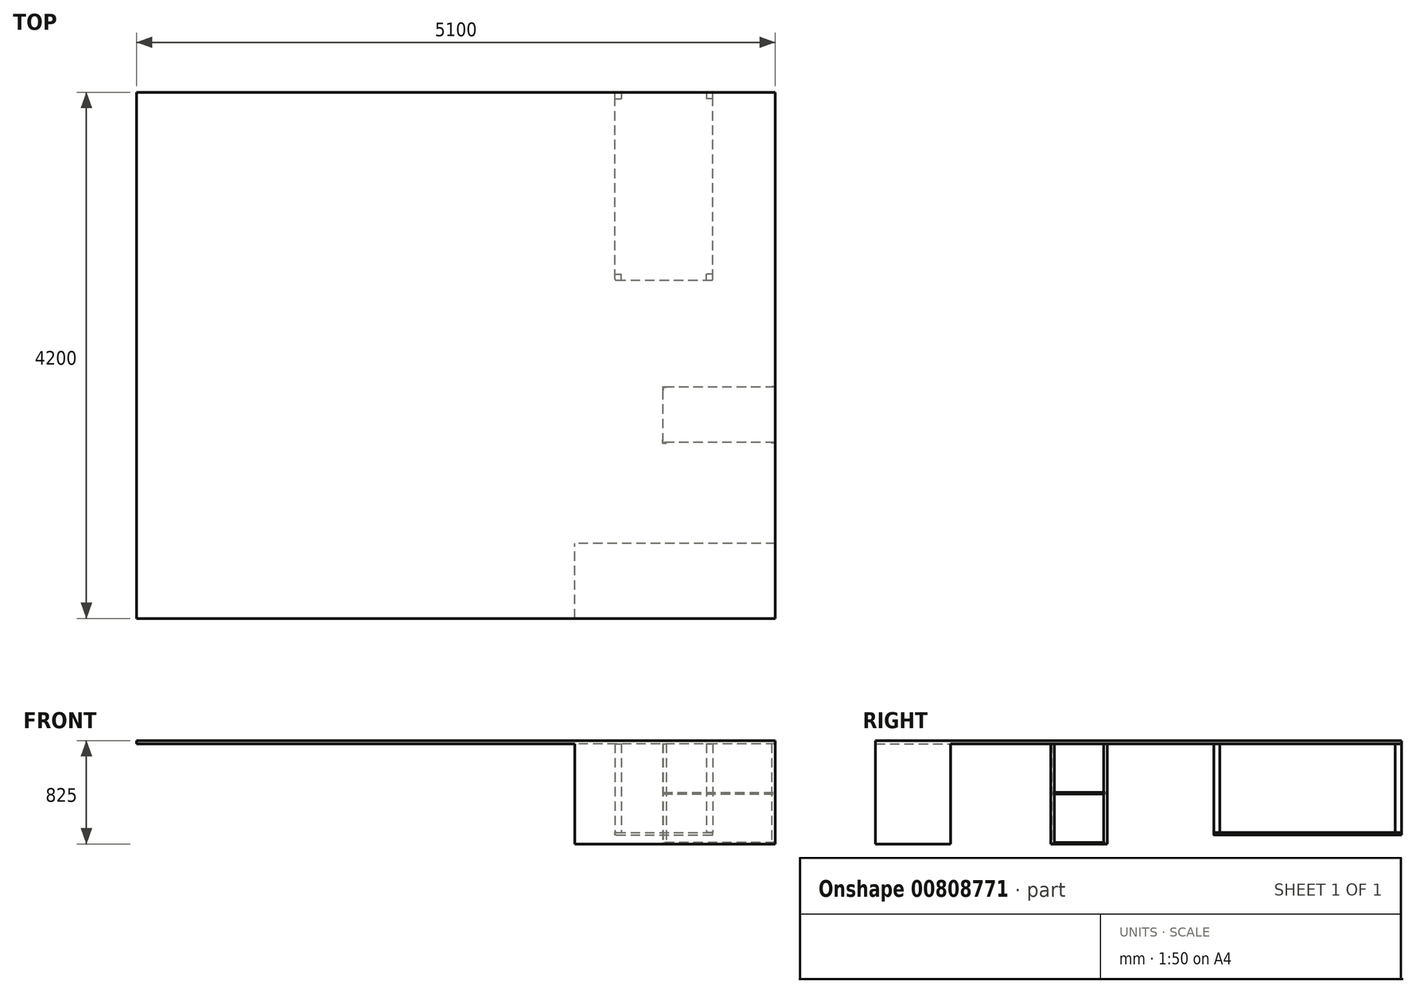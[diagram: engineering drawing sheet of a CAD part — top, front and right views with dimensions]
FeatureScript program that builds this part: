
annotation { "Feature Type Name" : "Feature", "Feature Type Description" : "" }
export const myFeature = defineFeature(function(context is Context, id is Id, definition is map)
    precondition{}
    {
        {
            var Q0;
            Q0=qCreatedBy(makeId("Top.planeOp"),FACE);
            var sketch = newSketch(context, id + "F0", { "sketchPlane" : qUnion([Q0])});
            skPoint(sketch, "E0.middle", {"position": v(0, 0) * mm});
            skLineSegment(sketch, "E1", {"start": v(-450, 225) * mm, "end": v(-450, 196) * mm});
            skLineSegment(sketch, "E2", {"start": v(-450, 225) * mm, "end": v(-421, 225) * mm});
            skLineSegment(sketch, "E3.0", {"start": v(-446, 221) * mm, "end": v(-421, 221) * mm});
            skLineSegment(sketch, "E3.1", {"start": v(-446, 221) * mm, "end": v(-446, 196) * mm});
            skLineSegment(sketch, "E4", {"start": v(-421, 225) * mm, "end": v(-421, 221) * mm});
            skLineSegment(sketch, "E5", {"start": v(-446, 196) * mm, "end": v(-450, 196) * mm});
            skLineSegment(sketch, "E6.bottom", {"start": v(0, 0) * mm, "end": v(-19.98, 0) * mm, "construction": true});
            skLineSegment(sketch, "E6.top", {"start": v(0, 2.25) * mm, "end": v(-19.98, 2.25) * mm, "construction": true});
            skLineSegment(sketch, "E6.left", {"start": v(0, 0) * mm, "end": v(0, 2.25) * mm, "construction": true});
            skLineSegment(sketch, "E6.right", {"start": v(-19.98, 0) * mm, "end": v(-19.98, 2.25) * mm, "construction": true});
            skLineSegment(sketch, "E7.MirrorCS", {"start": v(-446, -196) * mm, "end": v(-450, -196) * mm});
            skLineSegment(sketch, "E8.MirrorCS", {"start": v(-421, -225) * mm, "end": v(-421, -221) * mm});
            skLineSegment(sketch, "E9.MirrorCS", {"start": v(-450, -225) * mm, "end": v(-421, -225) * mm});
            skLineSegment(sketch, "E10.MirrorCS", {"start": v(-450, -225) * mm, "end": v(-450, -196) * mm});
            skLineSegment(sketch, "E11.MirrorCS", {"start": v(-446, -221) * mm, "end": v(-421, -221) * mm});
            skLineSegment(sketch, "E12.MirrorCS", {"start": v(-446, -221) * mm, "end": v(-446, -196) * mm});
            skLineSegment(sketch, "E13.MirrorCS", {"start": v(421, -225) * mm, "end": v(421, -221) * mm});
            skLineSegment(sketch, "E14.MirrorCS", {"start": v(446, -221) * mm, "end": v(421, -221) * mm});
            skLineSegment(sketch, "E15.MirrorCS", {"start": v(450, -225) * mm, "end": v(421, -225) * mm});
            skLineSegment(sketch, "E16.MirrorCS", {"start": v(446, -196) * mm, "end": v(450, -196) * mm});
            skLineSegment(sketch, "E17.MirrorCS", {"start": v(450, 225) * mm, "end": v(450, 196) * mm});
            skLineSegment(sketch, "E18.MirrorCS", {"start": v(446, 196) * mm, "end": v(450, 196) * mm});
            skLineSegment(sketch, "E19.MirrorCS", {"start": v(446, 221) * mm, "end": v(446, 196) * mm});
            skLineSegment(sketch, "E20.MirrorCS", {"start": v(446, 221) * mm, "end": v(421, 221) * mm});
            skLineSegment(sketch, "E21.MirrorCS", {"start": v(450, 225) * mm, "end": v(421, 225) * mm});
            skLineSegment(sketch, "E22.MirrorCS", {"start": v(450, -225) * mm, "end": v(450, -196) * mm});
            skLineSegment(sketch, "E23.MirrorCS", {"start": v(446, -221) * mm, "end": v(446, -196) * mm});
            skLineSegment(sketch, "E24.MirrorCS", {"start": v(421, 225) * mm, "end": v(421, 221) * mm});
            skSolve(sketch);
        }
        {
            var Q0;
            Q0 = qSketchRegion(id + "F0", true);
            extrude(context, id + "F1", {"entities" : qUnion([Q0]), "depth" : 800 * mm, "offsetDistance" : 25 * mm});
        }
        {
            var Q0;
            Q0=makeQuery(id+"F1.opExtrude","CAP_FACE",FACE,{"disambiguationData":[OSD([sQuery(id+"F0.wireOp",EDGE,"E13.MirrorCS"),sQuery(id+"F0.wireOp",EDGE,"E14.MirrorCS"),sQuery(id+"F0.wireOp",EDGE,"E15.MirrorCS"),sQuery(id+"F0.wireOp",EDGE,"E16.MirrorCS"),sQuery(id+"F0.wireOp",EDGE,"E22.MirrorCS"),sQuery(id+"F0.wireOp",EDGE,"E23.MirrorCS")])],"isStart":true});
            var sketch = newSketch(context, id + "F2", { "sketchPlane" : qUnion([Q0])});
            skLineSegment(sketch, "E25.bottom", {"start": v(446, 221) * mm, "end": v(-446, 221) * mm});
            skLineSegment(sketch, "E25.top", {"start": v(446, -221) * mm, "end": v(-446, -221) * mm});
            skLineSegment(sketch, "E25.left", {"start": v(446, 221) * mm, "end": v(446, -221) * mm});
            skLineSegment(sketch, "E25.right", {"start": v(-446, 221) * mm, "end": v(-446, -221) * mm});
            skSolve(sketch);
        }
        {
            var Q0;
            Q0 = qSketchRegion(id + "F2", true);
            extrude(context, id + "F3", {"entities" : qUnion([Q0]), "oppositeDirection" : true, "depth" : 10 * mm, "offsetDistance" : 25 * mm});
        }
        {
            var Q0;
            Q0=makeQuery(id+"F3.opExtrude","CAP_FACE",FACE,{"disambiguationData":[OSD([sQuery(id+"F2.wireOp",EDGE,"E25.bottom"),sQuery(id+"F2.wireOp",EDGE,"E25.top"),sQuery(id+"F2.wireOp",EDGE,"E25.left"),sQuery(id+"F2.wireOp",EDGE,"E25.right")])],"isStart":true});
            cPlane(context, id + "F4", {"entities" : qUnion([Q0]), "cplaneType" : CPlaneType.OFFSET, "offset" : 400 * mm, "oppositeDirection" : true, "width" : 150 * mm, "height" : 150 * mm});
        }
        {
            var Q0;
            Q0=qCreatedBy(id+"F4.planeOp",FACE);
            var sketch = newSketch(context, id + "F5", { "sketchPlane" : qUnion([Q0])});
            skLineSegment(sketch, "E26.0", {"start": v(446, -221) * mm, "end": v(446, 221) * mm});
            skLineSegment(sketch, "E26.1", {"start": v(-446, -221) * mm, "end": v(446, -221) * mm});
            skLineSegment(sketch, "E26.2", {"start": v(-446, 221) * mm, "end": v(-446, -221) * mm});
            skLineSegment(sketch, "E26.3", {"start": v(446, 221) * mm, "end": v(-446, 221) * mm});
            skSolve(sketch);
        }
        {
            var Q0;
            Q0 = qSketchRegion(id + "F5", true);
            extrude(context, id + "F6", {"entities" : qUnion([Q0]), "oppositeDirection" : true, "depth" : 10 * mm, "offsetDistance" : 25 * mm});
        }
        {
            var Q0;
            Q0=makeQuery(id+"F1.opExtrude","CAP_FACE",FACE,{"disambiguationData":[OSD([sQuery(id+"F0.wireOp",EDGE,"E1"),sQuery(id+"F0.wireOp",EDGE,"E2"),sQuery(id+"F0.wireOp",EDGE,"E3.0"),sQuery(id+"F0.wireOp",EDGE,"E3.1"),sQuery(id+"F0.wireOp",EDGE,"E4"),sQuery(id+"F0.wireOp",EDGE,"E5")])],"isStart":false});
            var sketch = newSketch(context, id + "F7", { "sketchPlane" : qUnion([Q0])});
            skLineSegment(sketch, "E27.bottom", {"start": v(450, 2575) * mm, "end": v(-4650, 2575) * mm});
            skLineSegment(sketch, "E27.top", {"start": v(450, -1625) * mm, "end": v(-4650, -1625) * mm});
            skLineSegment(sketch, "E27.left", {"start": v(450, 2575) * mm, "end": v(450, -1625) * mm});
            skLineSegment(sketch, "E27.right", {"start": v(-4650, 2575) * mm, "end": v(-4650, -1625) * mm});
            skLineSegment(sketch, "E28", {"start": v(450, -1025) * mm, "end": v(-4650, -1025) * mm, "construction": true});
            skSolve(sketch);
        }
        {
            var Q0;
            Q0 = qSketchRegion(id + "F7", true);
            extrude(context, id + "F8", {"entities" : qUnion([Q0]), "depth" : 25 * mm, "offsetDistance" : 25 * mm});
        }
        {
            var Q0;
            Q0=makeQuery(id+"F8.opExtrude","CAP_FACE",FACE,{"disambiguationData":[OSD([sQuery(id+"F7.wireOp",EDGE,"E27.bottom"),sQuery(id+"F7.wireOp",EDGE,"E27.top"),sQuery(id+"F7.wireOp",EDGE,"E27.left"),sQuery(id+"F7.wireOp",EDGE,"E27.right")])],"isStart":true});
            var sketch = newSketch(context, id + "F9", { "sketchPlane" : qUnion([Q0])});
            skLineSegment(sketch, "E29.bottom", {"start": v(450, 1625) * mm, "end": v(-1150, 1625) * mm});
            skLineSegment(sketch, "E29.top", {"start": v(450, 1025) * mm, "end": v(-1150, 1025) * mm});
            skLineSegment(sketch, "E29.left", {"start": v(450, 1625) * mm, "end": v(450, 1025) * mm});
            skLineSegment(sketch, "E29.right", {"start": v(-1150, 1625) * mm, "end": v(-1150, 1025) * mm});
            skSolve(sketch);
        }
        {
            var Q0;
            Q0 = qSketchRegion(id + "F9", true);
            extrude(context, id + "F10", {"entities" : qUnion([Q0]), "operationType" : NewBodyOperationType.ADD, "depth" : 800 * mm, "offsetDistance" : 25 * mm});
        }
        {
            var Q0;
            Q0=makeQuery(id+"F8.opExtrude","CAP_FACE",FACE,{"disambiguationData":[OSD([sQuery(id+"F7.wireOp",EDGE,"E27.bottom"),sQuery(id+"F7.wireOp",EDGE,"E27.top"),sQuery(id+"F7.wireOp",EDGE,"E27.left"),sQuery(id+"F7.wireOp",EDGE,"E27.right")])],"isStart":true});
            cPlane(context, id + "F11", {"entities" : qUnion([Q0]), "cplaneType" : CPlaneType.OFFSET, "offset" : 710 * mm, "width" : 150 * mm, "height" : 150 * mm});
        }
        {
            var Q0;
            Q0=qCreatedBy(id+"F11.planeOp",FACE);
            var sketch = newSketch(context, id + "F12", { "sketchPlane" : qUnion([Q0])});
            skLineSegment(sketch, "E30.bottom", {"start": v(-830, -1075) * mm, "end": v(-50, -1075) * mm});
            skLineSegment(sketch, "E30.top", {"start": v(-830, -2575) * mm, "end": v(-50, -2575) * mm});
            skLineSegment(sketch, "E30.left", {"start": v(-830, -1075) * mm, "end": v(-830, -2575) * mm});
            skLineSegment(sketch, "E30.right", {"start": v(-50, -1075) * mm, "end": v(-50, -2575) * mm});
            skSolve(sketch);
        }
        {
            var Q0;
            Q0 = qSketchRegion(id + "F12", true);
            extrude(context, id + "F13", {"entities" : qUnion([Q0]), "depth" : 18 * mm, "offsetDistance" : 25 * mm});
        }
        {
            var Q0;
            Q0=makeQuery(id+"F13.opExtrude","CAP_FACE",FACE,{"disambiguationData":[OSD([sQuery(id+"F12.wireOp",EDGE,"E30.bottom"),sQuery(id+"F12.wireOp",EDGE,"E30.top"),sQuery(id+"F12.wireOp",EDGE,"E30.left"),sQuery(id+"F12.wireOp",EDGE,"E30.right")])],"isStart":true});
            var sketch = newSketch(context, id + "F14", { "sketchPlane" : qUnion([Q0])});
            skLineSegment(sketch, "E31.bottom", {"start": v(-830, 1075) * mm, "end": v(-780, 1075) * mm});
            skLineSegment(sketch, "E31.top", {"start": v(-830, 1125) * mm, "end": v(-780, 1125) * mm});
            skLineSegment(sketch, "E31.left", {"start": v(-830, 1075) * mm, "end": v(-830, 1125) * mm});
            skLineSegment(sketch, "E31.right", {"start": v(-780, 1075) * mm, "end": v(-780, 1125) * mm});
            skLineSegment(sketch, "E32.bottom", {"start": v(-50, 1075) * mm, "end": v(-100, 1075) * mm});
            skLineSegment(sketch, "E32.top", {"start": v(-50, 1125) * mm, "end": v(-100, 1125) * mm});
            skLineSegment(sketch, "E32.left", {"start": v(-50, 1075) * mm, "end": v(-50, 1125) * mm});
            skLineSegment(sketch, "E32.right", {"start": v(-100, 1075) * mm, "end": v(-100, 1125) * mm});
            skLineSegment(sketch, "E33.bottom", {"start": v(-50, 2575) * mm, "end": v(-100, 2575) * mm});
            skLineSegment(sketch, "E33.top", {"start": v(-50, 2525) * mm, "end": v(-100, 2525) * mm});
            skLineSegment(sketch, "E33.left", {"start": v(-50, 2575) * mm, "end": v(-50, 2525) * mm});
            skLineSegment(sketch, "E33.right", {"start": v(-100, 2575) * mm, "end": v(-100, 2525) * mm});
            skLineSegment(sketch, "E34.bottom", {"start": v(-830, 2575) * mm, "end": v(-780, 2575) * mm});
            skLineSegment(sketch, "E34.top", {"start": v(-830, 2525) * mm, "end": v(-780, 2525) * mm});
            skLineSegment(sketch, "E34.left", {"start": v(-830, 2575) * mm, "end": v(-830, 2525) * mm});
            skLineSegment(sketch, "E34.right", {"start": v(-780, 2575) * mm, "end": v(-780, 2525) * mm});
            skSolve(sketch);
        }
        {
            var Q0;
            Q0 = qSketchRegion(id + "F14", true);
            var Q1;
            Q1=makeQuery(id+"F8.opExtrude","CAP_FACE",FACE,{"disambiguationData":[OSD([sQuery(id+"F7.wireOp",EDGE,"E27.bottom"),sQuery(id+"F7.wireOp",EDGE,"E27.top"),sQuery(id+"F7.wireOp",EDGE,"E27.left"),sQuery(id+"F7.wireOp",EDGE,"E27.right")])],"isStart":true});
            extrude(context, id + "F15", {"entities" : qUnion([Q0]), "endBound" : BoundingType.UP_TO_SURFACE, "depth" : 25 * mm, "endBoundEntityFace" : qUnion([Q1]), "offsetDistance" : 25 * mm});
        }
        {
            var Q0;
            Q0=makeQuery(id+"F13.opExtrude","SWEPT_EDGE",EDGE,{"disambiguationData":[OSD([sQuery(id+"F12.wireOp",EDGE,"E30.bottom"),sQuery(id+"F12.wireOp",EDGE,"E30.right")])]});
            var Q1;
            Q1=makeQuery(id+"F13.opExtrude","SWEPT_EDGE",EDGE,{"disambiguationData":[OSD([sQuery(id+"F12.wireOp",EDGE,"E30.top"),sQuery(id+"F12.wireOp",EDGE,"E30.right")])]});
            var Q2;
            Q2=makeQuery(id+"F13.opExtrude","SWEPT_EDGE",EDGE,{"disambiguationData":[OSD([sQuery(id+"F12.wireOp",EDGE,"E30.top"),sQuery(id+"F12.wireOp",EDGE,"E30.left")])]});
            var Q3;
            Q3=makeQuery(id+"F13.opExtrude","SWEPT_EDGE",EDGE,{"disambiguationData":[OSD([sQuery(id+"F12.wireOp",EDGE,"E30.bottom"),sQuery(id+"F12.wireOp",EDGE,"E30.left")])]});
            var Q4;
            Q4=makeQuery(id+"F15.opExtrude","SWEPT_EDGE",EDGE,{"disambiguationData":[OSD([sQuery(id+"F14.wireOp",EDGE,"E34.bottom"),sQuery(id+"F14.wireOp",EDGE,"E34.left")])]});
            var Q5;
            Q5=makeQuery(id+"F15.opExtrude","SWEPT_EDGE",EDGE,{"disambiguationData":[OSD([sQuery(id+"F14.wireOp",EDGE,"E33.bottom"),sQuery(id+"F14.wireOp",EDGE,"E33.left")])]});
            var Q6;
            Q6=makeQuery(id+"F15.opExtrude","SWEPT_EDGE",EDGE,{"disambiguationData":[OSD([sQuery(id+"F14.wireOp",EDGE,"E32.bottom"),sQuery(id+"F14.wireOp",EDGE,"E32.left")])]});
            var Q7;
            Q7=makeQuery(id+"F15.opExtrude","SWEPT_EDGE",EDGE,{"disambiguationData":[OSD([sQuery(id+"F14.wireOp",EDGE,"E31.bottom"),sQuery(id+"F14.wireOp",EDGE,"E31.left")])]});
            fillet(context, id + "F16", {"entities" : qUnion([Q0, Q1, Q2, Q3, Q4, Q5, Q6, Q7]), "radius" : 10 * mm, "tangentPropagation" : true, "allowEdgeOverflow" : false});
        }
    });
